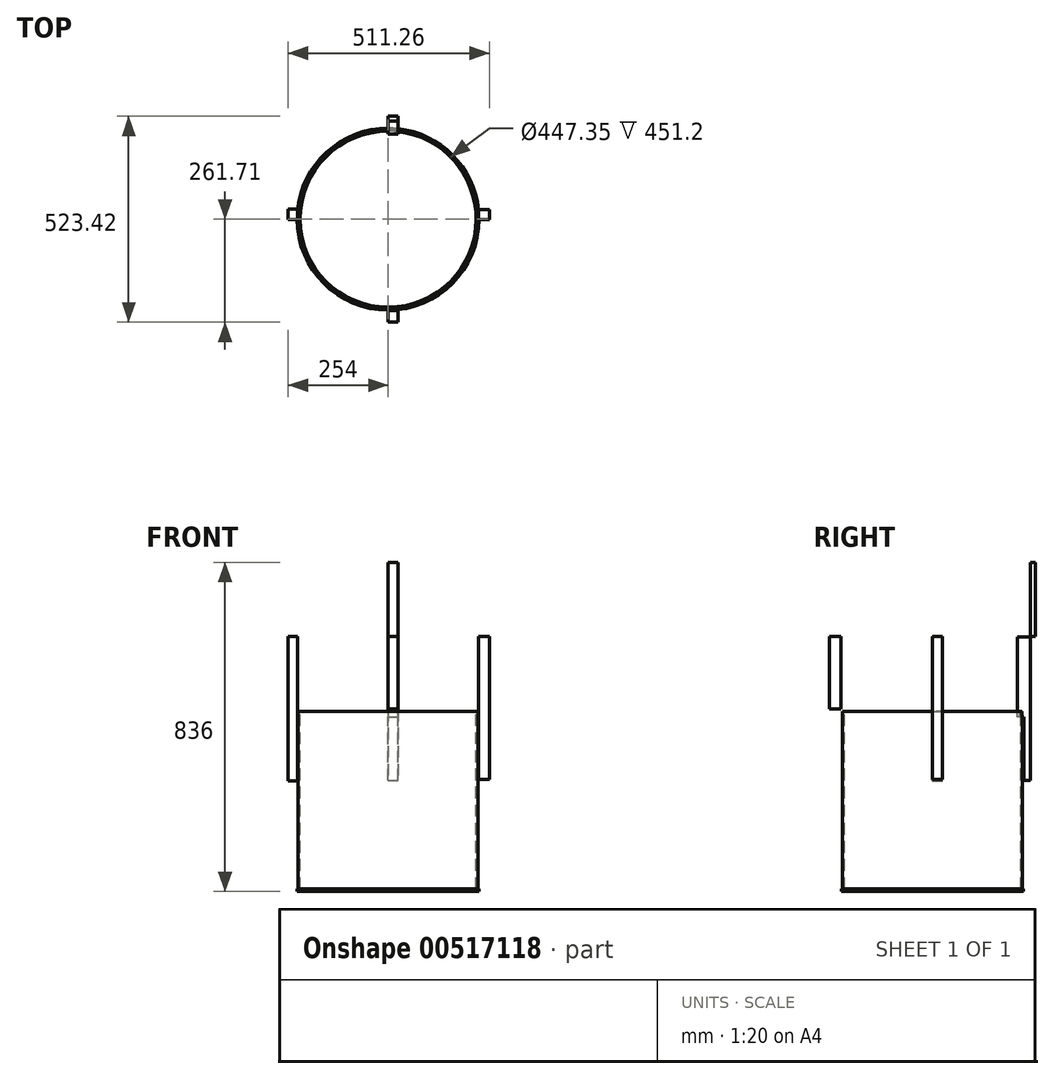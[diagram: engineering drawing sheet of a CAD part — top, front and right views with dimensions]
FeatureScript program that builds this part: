
annotation { "Feature Type Name" : "Feature", "Feature Type Description" : "" }
export const myFeature = defineFeature(function(context is Context, id is Id, definition is map)
    precondition{}
    {
        {
            var Q0;
            Q0=qCreatedBy(makeId("Top.planeOp"),FACE);
            var sketch = newSketch(context, id + "F0", { "sketchPlane" : qUnion([Q0])});
            skCircle(sketch, "E0", {"center": v(0, 0) * mm, "radius": 228.6 * mm});
            skSolve(sketch);
        }
        {
            var Q0;
            Q0=makeQuery(id+"F0.imprint","IMPRINT",FACE,{"disambiguationData":[TD([[makeQuery(id+"F0.imprint","IMPRINT",EDGE,{"derivedFrom":sQuery(id+"F0.wireOp",EDGE,"E0")}),1.0]])]});
            extrude(context, id + "F1", {"entities" : qUnion([Q0]), "depth" : 457.2 * mm, "offsetDistance" : 25 * mm});
        }
        {
            var Q0;
            Q0=makeQuery(id+"F1.opExtrude","CAP_FACE",FACE,{"disambiguationData":[OSD([sQuery(id+"F0.wireOp",EDGE,"E0")])],"isStart":false});
            var sketch = newSketch(context, id + "F2", { "sketchPlane" : qUnion([Q0])});
            skCircle(sketch, "E1", {"center": v(0, 0) * mm, "radius": 223.67 * mm});
            skSolve(sketch);
        }
        {
            var Q0;
            Q0=makeQuery(id+"F2.imprint","IMPRINT",FACE,{"disambiguationData":[TD([[makeQuery(id+"F2.imprint","IMPRINT",EDGE,{"derivedFrom":sQuery(id+"F2.wireOp",EDGE,"E1")}),1.0]])]});
            extrude(context, id + "F3", {"entities" : qUnion([Q0]), "operationType" : NewBodyOperationType.REMOVE, "endBound" : BoundingType.THROUGH_ALL, "oppositeDirection" : true, "depth" : 25 * mm, "offsetDistance" : 25 * mm});
        }
        {
            var Q0;
            Q0=qCreatedBy(makeId("Top.planeOp"),FACE);
            var sketch = newSketch(context, id + "F4", { "sketchPlane" : qUnion([Q0])});
            skCircle(sketch, "E2", {"center": v(0, 0) * mm, "radius": 231.18 * mm});
            skSolve(sketch);
        }
        {
            var Q0;
            Q0=makeQuery(id+"F4.imprint","IMPRINT",FACE,{"disambiguationData":[TD([[makeQuery(id+"F4.imprint","IMPRINT",EDGE,{"derivedFrom":sQuery(id+"F4.wireOp",EDGE,"E2")}),1.0]])]});
            extrude(context, id + "F5", {"entities" : qUnion([Q0]), "operationType" : NewBodyOperationType.ADD, "depth" : 6 * mm, "offsetDistance" : 25 * mm});
        }
        {
            var Q0;
            Q0=makeQuery(id+"F5.boolean.opBoolean","SPLIT",FACE,{"disambiguationData":[TD([makeQuery(id+"F3.boolean.opBoolean","COPY",FACE,{"derivedFrom":makeQuery(id+"F3.opExtrude","SWEPT_FACE",FACE,{"disambiguationData":[OSD([sQuery(id+"F2.wireOp",EDGE,"E1")])]})})])],"derivedFrom":makeQuery(id+"F5.opExtrude","CAP_FACE",FACE,{"disambiguationData":[OSD([sQuery(id+"F4.wireOp",EDGE,"E2")])],"isStart":false})});
            var sketch = newSketch(context, id + "F6", { "sketchPlane" : qUnion([Q0])});
            skLineSegment(sketch, "E3.bottom", {"start": v(0, 213.78) * mm, "end": v(25.26, 213.78) * mm});
            skLineSegment(sketch, "E3.top", {"start": v(0, 192.22) * mm, "end": v(25.26, 192.22) * mm});
            skLineSegment(sketch, "E3.left", {"start": v(0, 213.78) * mm, "end": v(0, 192.22) * mm});
            skLineSegment(sketch, "E3.right", {"start": v(25.26, 213.78) * mm, "end": v(25.26, 192.22) * mm});
            skSolve(sketch);
        }
        {
            var Q0;
            Q0=makeQuery(id+"F6.imprint","IMPRINT",FACE,{"disambiguationData":[TD([[makeQuery(id+"F6.imprint","IMPRINT",EDGE,{"derivedFrom":sQuery(id+"F6.wireOp",EDGE,"E3.bottom")}),-1.0]])]});
            extrude(context, id + "F7", {"entities" : qUnion([Q0]), "operationType" : NewBodyOperationType.ADD, "depth" : 458 * mm, "offsetDistance" : 25 * mm});
        }
        {
            var Q0;
            Q0=makeQuery(id+"F7.opExtrude","SWEPT_FACE",FACE,{"disambiguationData":[OSD([sQuery(id+"F6.wireOp",EDGE,"E3.bottom")])]});
            var sketch = newSketch(context, id + "F8", { "sketchPlane" : qUnion([Q0])});
            skLineSegment(sketch, "E4.bottom", {"start": v(0, 464) * mm, "end": v(-25.26, 464) * mm});
            skLineSegment(sketch, "E4.top", {"start": v(0, 443.28) * mm, "end": v(-25.26, 443.28) * mm});
            skLineSegment(sketch, "E4.left", {"start": v(0, 464) * mm, "end": v(0, 443.28) * mm});
            skLineSegment(sketch, "E4.right", {"start": v(-25.26, 464) * mm, "end": v(-25.26, 443.28) * mm});
            skSolve(sketch);
        }
        {
            var Q0;
            Q0=makeQuery(id+"F8.imprint","IMPRINT",FACE,{"disambiguationData":[TD([[makeQuery(id+"F8.imprint","IMPRINT",EDGE,{"derivedFrom":sQuery(id+"F8.wireOp",EDGE,"E4.bottom")}),1.0]])]});
            extrude(context, id + "F9", {"entities" : qUnion([Q0]), "operationType" : NewBodyOperationType.ADD, "depth" : 35 * mm, "offsetDistance" : 25 * mm});
        }
        {
            var Q0;
            Q0=makeQuery(id+"F9.boolean.opBoolean","MERGE",FACE,{"derivedFrom":[makeQuery(id+"F7.opExtrude","CAP_FACE",FACE,{"disambiguationData":[OSD([sQuery(id+"F6.wireOp",EDGE,"E3.bottom"),sQuery(id+"F6.wireOp",EDGE,"E3.top"),sQuery(id+"F6.wireOp",EDGE,"E3.left"),sQuery(id+"F6.wireOp",EDGE,"E3.right")])],"isStart":false}),makeQuery(id+"F9.opExtrude","SWEPT_FACE",FACE,{"disambiguationData":[OSD([sQuery(id+"F8.wireOp",EDGE,"E4.bottom")])]})]});
            var sketch = newSketch(context, id + "F10", { "sketchPlane" : qUnion([Q0])});
            skLineSegment(sketch, "E5.bottom", {"start": v(0, 215.79) * mm, "end": v(25.26, 215.79) * mm});
            skLineSegment(sketch, "E5.top", {"start": v(0, 192.22) * mm, "end": v(25.26, 192.22) * mm});
            skLineSegment(sketch, "E5.left", {"start": v(0, 215.79) * mm, "end": v(0, 192.22) * mm});
            skLineSegment(sketch, "E5.right", {"start": v(25.26, 215.79) * mm, "end": v(25.26, 192.22) * mm});
            skSolve(sketch);
        }
        {
            var Q0;
            Q0=makeQuery(id+"F10.imprint","IMPRINT",FACE,{"disambiguationData":[TD([[makeQuery(id+"F10.imprint","IMPRINT",EDGE,{"derivedFrom":sQuery(id+"F10.wireOp",EDGE,"E5.bottom")}),-1.0]])]});
            extrude(context, id + "F11", {"entities" : qUnion([Q0]), "operationType" : NewBodyOperationType.REMOVE, "endBound" : BoundingType.THROUGH_ALL, "oppositeDirection" : true, "depth" : 226 * mm, "offsetDistance" : 25 * mm});
        }
        {
            var Q0;
            {var subQ2=sQuery(id+"F8.wireOp",EDGE,"E4.top");Q0=makeQuery(id+"F9.boolean.opBoolean","SPLIT",FACE,{"disambiguationData":[TD([makeQuery(id+"F1.opExtrude","SWEPT_FACE",FACE,{"disambiguationData":[OSD([sQuery(id+"F0.wireOp",EDGE,"E0")])]})])],"derivedFrom":makeQuery(id+"F9.opExtrude","SWEPT_FACE",FACE,{"disambiguationData":[OSD([subQ2])]})});}
            var sketch = newSketch(context, id + "F12", { "sketchPlane" : qUnion([Q0])});
            skLineSegment(sketch, "E6.bottom", {"start": v(0, -231.23) * mm, "end": v(25.26, -231.23) * mm});
            skLineSegment(sketch, "E6.top", {"start": v(0, -248.78) * mm, "end": v(25.26, -248.78) * mm});
            skLineSegment(sketch, "E6.left", {"start": v(0, -231.23) * mm, "end": v(0, -248.78) * mm});
            skLineSegment(sketch, "E6.right", {"start": v(25.26, -231.23) * mm, "end": v(25.26, -248.78) * mm});
            skSolve(sketch);
        }
        {
            var Q0;
            Q0=makeQuery(id+"F12.imprint","IMPRINT",FACE,{"disambiguationData":[TD([[makeQuery(id+"F12.imprint","IMPRINT",EDGE,{"derivedFrom":sQuery(id+"F12.wireOp",EDGE,"E6.bottom")}),-1.0]])]});
            extrude(context, id + "F13", {"entities" : qUnion([Q0]), "operationType" : NewBodyOperationType.ADD, "depth" : 162 * mm, "offsetDistance" : 25 * mm});
        }
        {
            var Q0;
            Q0=makeQuery(id+"F9.boolean.opBoolean","MERGE",FACE,{"derivedFrom":[makeQuery(id+"F7.opExtrude","CAP_FACE",FACE,{"disambiguationData":[OSD([sQuery(id+"F6.wireOp",EDGE,"E3.bottom"),sQuery(id+"F6.wireOp",EDGE,"E3.top"),sQuery(id+"F6.wireOp",EDGE,"E3.left"),sQuery(id+"F6.wireOp",EDGE,"E3.right")])],"isStart":false}),makeQuery(id+"F9.opExtrude","SWEPT_FACE",FACE,{"disambiguationData":[OSD([sQuery(id+"F8.wireOp",EDGE,"E4.bottom")])]})]});
            var sketch = newSketch(context, id + "F14", { "sketchPlane" : qUnion([Q0])});
            skLineSegment(sketch, "E7.bottom", {"start": v(0, 248.78) * mm, "end": v(25.26, 248.78) * mm});
            skLineSegment(sketch, "E7.top", {"start": v(0, 232.29) * mm, "end": v(25.26, 232.29) * mm});
            skLineSegment(sketch, "E7.left", {"start": v(0, 248.78) * mm, "end": v(0, 232.29) * mm});
            skLineSegment(sketch, "E7.right", {"start": v(25.26, 248.78) * mm, "end": v(25.26, 232.29) * mm});
            skSolve(sketch);
        }
        {
            var Q0;
            Q0=makeQuery(id+"F14.imprint","IMPRINT",FACE,{"disambiguationData":[TD([[makeQuery(id+"F14.imprint","IMPRINT",EDGE,{"derivedFrom":sQuery(id+"F14.wireOp",EDGE,"E7.bottom")}),-1.0]])]});
            extrude(context, id + "F15", {"entities" : qUnion([Q0]), "operationType" : NewBodyOperationType.ADD, "depth" : 183 * mm, "offsetDistance" : 25 * mm});
        }
        {
            var Q0;
            Q0=makeQuery(id+"F15.opExtrude","SWEPT_FACE",FACE,{"disambiguationData":[OSD([sQuery(id+"F14.wireOp",EDGE,"E7.top")])]});
            extrude(context, id + "F16", {"entities" : qUnion([Q0]), "operationType" : NewBodyOperationType.ADD, "depth" : 494 * mm, "offsetDistance" : 25 * mm});
        }
        {
            var Q0;
            {var subQ0=sQuery(id+"F14.wireOp",EDGE,"E7.top");Q0=makeQuery(id+"F16.opExtrude","SWEPT_FACE",FACE,{"disambiguationData":[OSD([subQ0]),TDD([makeQuery(id+"F15.opExtrude","CAP_EDGE",EDGE,{"disambiguationData":[OSD([subQ0])],"isStart":true})])]});}
            var sketch = newSketch(context, id + "F17", { "sketchPlane" : qUnion([Q0])});
            skLineSegment(sketch, "E8.bottom", {"start": v(0, 261.71) * mm, "end": v(25.26, 261.71) * mm});
            skLineSegment(sketch, "E8.top", {"start": v(0, 232.66) * mm, "end": v(25.26, 232.66) * mm});
            skLineSegment(sketch, "E8.left", {"start": v(0, 261.71) * mm, "end": v(0, 232.66) * mm});
            skLineSegment(sketch, "E8.right", {"start": v(25.26, 261.71) * mm, "end": v(25.26, 232.66) * mm});
            skSolve(sketch);
        }
        {
            var Q0;
            Q0=makeQuery(id+"F17.imprint","IMPRINT",FACE,{"disambiguationData":[TD([[makeQuery(id+"F17.imprint","IMPRINT",EDGE,{"derivedFrom":sQuery(id+"F17.wireOp",EDGE,"E8.bottom")}),-1.0]])]});
            extrude(context, id + "F18", {"entities" : qUnion([Q0]), "operationType" : NewBodyOperationType.ADD, "depth" : 189 * mm, "offsetDistance" : 25 * mm});
        }
        {
            var Q0;
            {var subQ0=sQuery(id+"F14.wireOp",EDGE,"E7.right");var subQ1=sQuery(id+"F8.wireOp",EDGE,"E4.right");var subQ2=sQuery(id+"F6.wireOp",EDGE,"E3.right");Q0=makeQuery(id+"F18.boolean.opBoolean","MERGE",FACE,{"derivedFrom":[makeQuery(id+"F16.boolean.opBoolean","MERGE",FACE,{"derivedFrom":[makeQuery(id+"F15.boolean.opBoolean","MERGE",FACE,{"derivedFrom":[makeQuery(id+"F13.boolean.opBoolean","MERGE",FACE,{"derivedFrom":[makeQuery(id+"F9.boolean.opBoolean","MERGE",FACE,{"derivedFrom":[makeQuery(id+"F7.opExtrude","SWEPT_FACE",FACE,{"disambiguationData":[OSD([subQ2])]}),makeQuery(id+"F9.opExtrude","SWEPT_FACE",FACE,{"disambiguationData":[OSD([subQ1])]})]}),makeQuery(id+"F13.opExtrude","SWEPT_FACE",FACE,{"disambiguationData":[OSD([sQuery(id+"F12.wireOp",EDGE,"E6.right")])]})]}),makeQuery(id+"F15.opExtrude","SWEPT_FACE",FACE,{"disambiguationData":[OSD([subQ0])]})]}),makeQuery(id+"F16.opExtrude","SWEPT_FACE",FACE,{"disambiguationData":[OSD([subQ2,sQuery(id+"F8.wireOp",EDGE,"E4.bottom"),subQ1,sQuery(id+"F14.wireOp",EDGE,"E7.top"),subQ0])]})]}),makeQuery(id+"F18.opExtrude","SWEPT_FACE",FACE,{"disambiguationData":[OSD([sQuery(id+"F17.wireOp",EDGE,"E8.right")])]})]});}
            var sketch = newSketch(context, id + "F19", { "sketchPlane" : qUnion([Q0])});
            skLineSegment(sketch, "E9.bottom", {"start": v(-232.66, 464) * mm, "end": v(222.5, 464) * mm});
            skLineSegment(sketch, "E9.top", {"start": v(-232.66, 647) * mm, "end": v(222.5, 647) * mm});
            skLineSegment(sketch, "E9.left", {"start": v(-232.66, 464) * mm, "end": v(-232.66, 647) * mm});
            skLineSegment(sketch, "E9.right", {"start": v(222.5, 464) * mm, "end": v(222.5, 647) * mm});
            skSolve(sketch);
        }
        {
            var Q0;
            Q0=makeQuery(id+"F19.imprint","IMPRINT",FACE,{"disambiguationData":[TD([[makeQuery(id+"F19.imprint","IMPRINT",EDGE,{"derivedFrom":sQuery(id+"F19.wireOp",EDGE,"E9.top")}),1.0]])]});
            extrude(context, id + "F20", {"entities" : qUnion([Q0]), "operationType" : NewBodyOperationType.REMOVE, "endBound" : BoundingType.THROUGH_ALL, "oppositeDirection" : true, "depth" : 25 * mm, "offsetDistance" : 25 * mm});
        }
        {
            var Q0;
            Q0=makeQuery(id+"F11.boolean.opBoolean","COPY",FACE,{"derivedFrom":makeQuery(id+"F11.opExtrude","SWEPT_FACE",FACE,{"disambiguationData":[OSD([sQuery(id+"F10.wireOp",EDGE,"E5.top")])]})});
            extrude(context, id + "F21", {"entities" : qUnion([Q0]), "operationType" : NewBodyOperationType.ADD, "depth" : 25 * mm, "offsetDistance" : 25 * mm});
        }
        {
            var Q0;
            Q0=makeQuery(id+"F20.boolean.opBoolean","COPY",FACE,{"derivedFrom":makeQuery(id+"F20.opExtrude","SWEPT_FACE",FACE,{"disambiguationData":[OSD([sQuery(id+"F19.wireOp",EDGE,"E9.right")])]})});
            extrude(context, id + "F22", {"entities" : qUnion([Q0]), "operationType" : NewBodyOperationType.ADD, "depth" : 223 * mm, "offsetDistance" : 25 * mm});
        }
        {
            var Q0;
            {var subQ0=sQuery(id+"F19.wireOp",EDGE,"E9.right");var subQ2=sQuery(id+"F12.wireOp",EDGE,"E6.right");var subQ5=sQuery(id+"F0.wireOp",EDGE,"E0");var subQ8=sQuery(id+"F6.wireOp",EDGE,"E3.right");var subQ9=makeQuery(id+"F7.opExtrude","SWEPT_FACE",FACE,{"disambiguationData":[OSD([subQ8])]});var subQ10=sQuery(id+"F8.wireOp",EDGE,"E4.bottom");var subQ13=sQuery(id+"F8.wireOp",EDGE,"E4.right");var subQ14=makeQuery(id+"F9.opExtrude","SWEPT_FACE",FACE,{"disambiguationData":[OSD([subQ13])]});var subQ15=sQuery(id+"F14.wireOp",EDGE,"E7.right");var subQ16=sQuery(id+"F14.wireOp",EDGE,"E7.top");Q0=makeQuery(id+"F22.boolean.opBoolean","MERGE",FACE,{"derivedFrom":[makeQuery(id+"F20.boolean.opBoolean","SPLIT",FACE,{"disambiguationData":[TD([makeQuery(id+"F1.opExtrude","SWEPT_FACE",FACE,{"disambiguationData":[OSD([subQ5])]})])],"derivedFrom":makeQuery(id+"F18.boolean.opBoolean","MERGE",FACE,{"derivedFrom":[makeQuery(id+"F16.boolean.opBoolean","MERGE",FACE,{"derivedFrom":[makeQuery(id+"F15.boolean.opBoolean","MERGE",FACE,{"derivedFrom":[makeQuery(id+"F13.boolean.opBoolean","MERGE",FACE,{"derivedFrom":[makeQuery(id+"F9.boolean.opBoolean","MERGE",FACE,{"derivedFrom":[subQ9,subQ14]}),makeQuery(id+"F13.opExtrude","SWEPT_FACE",FACE,{"disambiguationData":[OSD([subQ2])]})]}),makeQuery(id+"F15.opExtrude","SWEPT_FACE",FACE,{"disambiguationData":[OSD([subQ15])]})]}),makeQuery(id+"F16.opExtrude","SWEPT_FACE",FACE,{"disambiguationData":[OSD([subQ8,subQ10,subQ13,subQ16,subQ15])]})]}),makeQuery(id+"F18.opExtrude","SWEPT_FACE",FACE,{"disambiguationData":[OSD([sQuery(id+"F17.wireOp",EDGE,"E8.right")])]})]})}),makeQuery(id+"F22.opExtrude","SWEPT_FACE",FACE,{"disambiguationData":[OSD([subQ0])]})]});}
            var sketch = newSketch(context, id + "F23", { "sketchPlane" : qUnion([Q0])});
            skLineSegment(sketch, "E10.bottom", {"start": v(-0.5, 647) * mm, "end": v(24.32, 647) * mm});
            skLineSegment(sketch, "E10.top", {"start": v(-0.5, 464) * mm, "end": v(24.32, 464) * mm});
            skLineSegment(sketch, "E10.left", {"start": v(-0.5, 647) * mm, "end": v(-0.5, 464) * mm});
            skLineSegment(sketch, "E10.right", {"start": v(24.32, 647) * mm, "end": v(24.32, 464) * mm});
            skSolve(sketch);
        }
        {
            var Q0;
            Q0=makeQuery(id+"F23.imprint","IMPRINT",FACE,{"disambiguationData":[TD([[makeQuery(id+"F23.imprint","IMPRINT",EDGE,{"derivedFrom":sQuery(id+"F23.wireOp",EDGE,"E10.bottom")}),1.0]])]});
            extrude(context, id + "F24", {"entities" : qUnion([Q0]), "operationType" : NewBodyOperationType.ADD, "depth" : 232 * mm, "offsetDistance" : 25 * mm});
        }
        {
            var Q0;
            Q0=makeQuery(id+"F24.opExtrude","SWEPT_FACE",FACE,{"disambiguationData":[OSD([sQuery(id+"F23.wireOp",EDGE,"E10.right")])]});
            var sketch = newSketch(context, id + "F25", { "sketchPlane" : qUnion([Q0])});
            skLineSegment(sketch, "E11.bottom", {"start": v(-257.26, 647) * mm, "end": v(-229.4, 647) * mm});
            skLineSegment(sketch, "E11.top", {"start": v(-257.26, 464) * mm, "end": v(-229.4, 464) * mm});
            skLineSegment(sketch, "E11.left", {"start": v(-257.26, 647) * mm, "end": v(-257.26, 464) * mm});
            skLineSegment(sketch, "E11.right", {"start": v(-229.4, 647) * mm, "end": v(-229.4, 464) * mm});
            skSolve(sketch);
        }
        {
            var Q0;
            {var subQ0=sQuery(id+"F25.wireOp",EDGE,"E11.right");Q0=makeQuery(id+"F25.imprint","IMPRINT",FACE,{"disambiguationData":[TD([[makeQuery(id+"F25.imprint","IMPRINT",EDGE,{"derivedFrom":subQ0}),1.0]])]});}
            extrude(context, id + "F26", {"entities" : qUnion([Q0]), "operationType" : NewBodyOperationType.REMOVE, "endBound" : BoundingType.THROUGH_ALL, "oppositeDirection" : true, "depth" : 25 * mm, "offsetDistance" : 25 * mm});
        }
        {
            var Q0;
            {var subQ0=sQuery(id+"F23.wireOp",EDGE,"E10.right");var subQ2=sQuery(id+"F23.wireOp",EDGE,"E10.top");var subQ3=sQuery(id+"F19.wireOp",EDGE,"E9.right");Q0=makeQuery(id+"F26.boolean.opBoolean","SPLIT",FACE,{"disambiguationData":[TD([makeQuery(id+"F24.opExtrude","SWEPT_FACE",FACE,{"disambiguationData":[OSD([subQ0])]})])],"derivedFrom":makeQuery(id+"F24.boolean.opBoolean","MERGE",FACE,{"derivedFrom":[makeQuery(id+"F22.opExtrude","SWEPT_FACE",FACE,{"disambiguationData":[OSD([sQuery(id+"F19.wireOp",EDGE,"E9.bottom"),subQ3])]}),makeQuery(id+"F24.opExtrude","SWEPT_FACE",FACE,{"disambiguationData":[OSD([subQ2])]})]})});}
            extrude(context, id + "F27", {"entities" : qUnion([Q0]), "operationType" : NewBodyOperationType.ADD, "depth" : 180 * mm, "offsetDistance" : 25 * mm});
        }
        {
            var Q0;
            {var subQ0=sQuery(id+"F19.wireOp",EDGE,"E9.right");var subQ1=sQuery(id+"F17.wireOp",EDGE,"E8.left");var subQ2=sQuery(id+"F14.wireOp",EDGE,"E7.left");var subQ3=sQuery(id+"F14.wireOp",EDGE,"E7.top");var subQ4=sQuery(id+"F12.wireOp",EDGE,"E6.left");var subQ5=sQuery(id+"F8.wireOp",EDGE,"E4.left");var subQ6=sQuery(id+"F8.wireOp",EDGE,"E4.bottom");var subQ7=sQuery(id+"F6.wireOp",EDGE,"E3.left");var subQ11=sQuery(id+"F0.wireOp",EDGE,"E0");var subQ15=makeQuery(id+"F7.opExtrude","SWEPT_FACE",FACE,{"disambiguationData":[OSD([subQ7])]});var subQ16=makeQuery(id+"F9.opExtrude","SWEPT_FACE",FACE,{"disambiguationData":[OSD([subQ5])]});Q0=makeQuery(id+"F22.boolean.opBoolean","MERGE",FACE,{"derivedFrom":[makeQuery(id+"F20.boolean.opBoolean","SPLIT",FACE,{"disambiguationData":[TD([makeQuery(id+"F1.opExtrude","SWEPT_FACE",FACE,{"disambiguationData":[OSD([subQ11])]})])],"derivedFrom":makeQuery(id+"F18.boolean.opBoolean","MERGE",FACE,{"derivedFrom":[makeQuery(id+"F16.boolean.opBoolean","MERGE",FACE,{"derivedFrom":[makeQuery(id+"F15.boolean.opBoolean","MERGE",FACE,{"derivedFrom":[makeQuery(id+"F13.boolean.opBoolean","MERGE",FACE,{"derivedFrom":[makeQuery(id+"F9.boolean.opBoolean","MERGE",FACE,{"derivedFrom":[subQ15,subQ16]}),makeQuery(id+"F13.opExtrude","SWEPT_FACE",FACE,{"disambiguationData":[OSD([subQ4])]})]}),makeQuery(id+"F15.opExtrude","SWEPT_FACE",FACE,{"disambiguationData":[OSD([subQ2])]})]}),makeQuery(id+"F16.opExtrude","SWEPT_FACE",FACE,{"disambiguationData":[OSD([subQ7,subQ6,subQ5,subQ3,subQ2])]})]}),makeQuery(id+"F18.opExtrude","SWEPT_FACE",FACE,{"disambiguationData":[OSD([subQ1])]})]})}),makeQuery(id+"F22.opExtrude","SWEPT_FACE",FACE,{"disambiguationData":[OSD([subQ7,subQ6,subQ5,subQ4,subQ3,subQ2,subQ1,subQ0])]})]});}
            var sketch = newSketch(context, id + "F28", { "sketchPlane" : qUnion([Q0])});
            skLineSegment(sketch, "E12.bottom", {"start": v(0.5, 464) * mm, "end": v(-25.28, 464) * mm});
            skLineSegment(sketch, "E12.top", {"start": v(0.5, 647) * mm, "end": v(-25.28, 647) * mm});
            skLineSegment(sketch, "E12.left", {"start": v(0.5, 464) * mm, "end": v(0.5, 647) * mm});
            skLineSegment(sketch, "E12.right", {"start": v(-25.28, 464) * mm, "end": v(-25.28, 647) * mm});
            skSolve(sketch);
        }
        {
            var Q0;
            Q0=makeQuery(id+"F28.imprint","IMPRINT",FACE,{"disambiguationData":[TD([[makeQuery(id+"F28.imprint","IMPRINT",EDGE,{"derivedFrom":sQuery(id+"F28.wireOp",EDGE,"E12.bottom")}),-1.0]])]});
            extrude(context, id + "F29", {"entities" : qUnion([Q0]), "operationType" : NewBodyOperationType.ADD, "depth" : 254 * mm, "offsetDistance" : 25 * mm});
        }
        {
            var Q0;
            {var subQ4=sQuery(id+"F6.wireOp",EDGE,"E3.left");var subQ7=sQuery(id+"F19.wireOp",EDGE,"E9.right");Q0=makeQuery(id+"F29.boolean.opBoolean","MERGE",FACE,{"derivedFrom":[makeQuery(id+"F26.boolean.opBoolean","SPLIT",FACE,{"disambiguationData":[TD([makeQuery(id+"F7.opExtrude","SWEPT_FACE",FACE,{"disambiguationData":[OSD([subQ4])]})])],"derivedFrom":makeQuery(id+"F24.boolean.opBoolean","MERGE",FACE,{"derivedFrom":[makeQuery(id+"F22.opExtrude","CAP_FACE",FACE,{"disambiguationData":[OSD([subQ7])],"isStart":false}),makeQuery(id+"F24.opExtrude","SWEPT_FACE",FACE,{"disambiguationData":[OSD([sQuery(id+"F23.wireOp",EDGE,"E10.left")])]})]})}),makeQuery(id+"F29.opExtrude","SWEPT_FACE",FACE,{"disambiguationData":[OSD([sQuery(id+"F28.wireOp",EDGE,"E12.left")])]})]});}
            var sketch = newSketch(context, id + "F30", { "sketchPlane" : qUnion([Q0])});
            skLineSegment(sketch, "E13.bottom", {"start": v(-254, 647) * mm, "end": v(-230.36, 647) * mm});
            skLineSegment(sketch, "E13.top", {"start": v(-254, 464) * mm, "end": v(-230.36, 464) * mm});
            skLineSegment(sketch, "E13.left", {"start": v(-254, 647) * mm, "end": v(-254, 464) * mm});
            skLineSegment(sketch, "E13.right", {"start": v(-230.36, 647) * mm, "end": v(-230.36, 464) * mm});
            skSolve(sketch);
        }
        {
            var Q0;
            {var subQ0=sQuery(id+"F30.wireOp",EDGE,"E13.right");Q0=makeQuery(id+"F30.imprint","IMPRINT",FACE,{"disambiguationData":[TD([[makeQuery(id+"F30.imprint","IMPRINT",EDGE,{"derivedFrom":subQ0}),1.0]])]});}
            extrude(context, id + "F31", {"entities" : qUnion([Q0]), "operationType" : NewBodyOperationType.REMOVE, "endBound" : BoundingType.THROUGH_ALL, "oppositeDirection" : true, "depth" : 25 * mm, "offsetDistance" : 25 * mm});
        }
        {
            var Q0;
            {var subQ4=sQuery(id+"F6.wireOp",EDGE,"E3.left");var subQ7=sQuery(id+"F19.wireOp",EDGE,"E9.right");var subQ11=makeQuery(id+"F7.opExtrude","SWEPT_FACE",FACE,{"disambiguationData":[OSD([subQ4])]});Q0=makeQuery(id+"F29.boolean.opBoolean","MERGE",FACE,{"derivedFrom":[makeQuery(id+"F26.boolean.opBoolean","SPLIT",FACE,{"disambiguationData":[TD([subQ11])],"derivedFrom":makeQuery(id+"F24.boolean.opBoolean","MERGE",FACE,{"derivedFrom":[makeQuery(id+"F22.opExtrude","SWEPT_FACE",FACE,{"disambiguationData":[OSD([sQuery(id+"F19.wireOp",EDGE,"E9.bottom"),subQ7])]}),makeQuery(id+"F24.opExtrude","SWEPT_FACE",FACE,{"disambiguationData":[OSD([sQuery(id+"F23.wireOp",EDGE,"E10.top")])]})]})}),makeQuery(id+"F29.opExtrude","SWEPT_FACE",FACE,{"disambiguationData":[OSD([sQuery(id+"F28.wireOp",EDGE,"E12.bottom")])]})]});}
            extrude(context, id + "F32", {"entities" : qUnion([Q0]), "operationType" : NewBodyOperationType.ADD, "depth" : 184 * mm, "offsetDistance" : 25 * mm});
        }
        {
            var Q0;
            Q0=makeQuery(id+"F31.boolean.opBoolean","COPY",FACE,{"derivedFrom":makeQuery(id+"F31.opExtrude","SWEPT_FACE",FACE,{"disambiguationData":[OSD([sQuery(id+"F19.wireOp",EDGE,"E9.bottom"),sQuery(id+"F19.wireOp",EDGE,"E9.right"),sQuery(id+"F23.wireOp",EDGE,"E10.top"),sQuery(id+"F23.wireOp",EDGE,"E10.left"),sQuery(id+"F28.wireOp",EDGE,"E12.bottom"),sQuery(id+"F28.wireOp",EDGE,"E12.left")])]})});
            extrude(context, id + "F33", {"entities" : qUnion([Q0]), "operationType" : NewBodyOperationType.ADD, "depth" : 182 * mm, "offsetDistance" : 25 * mm});
        }
    });
